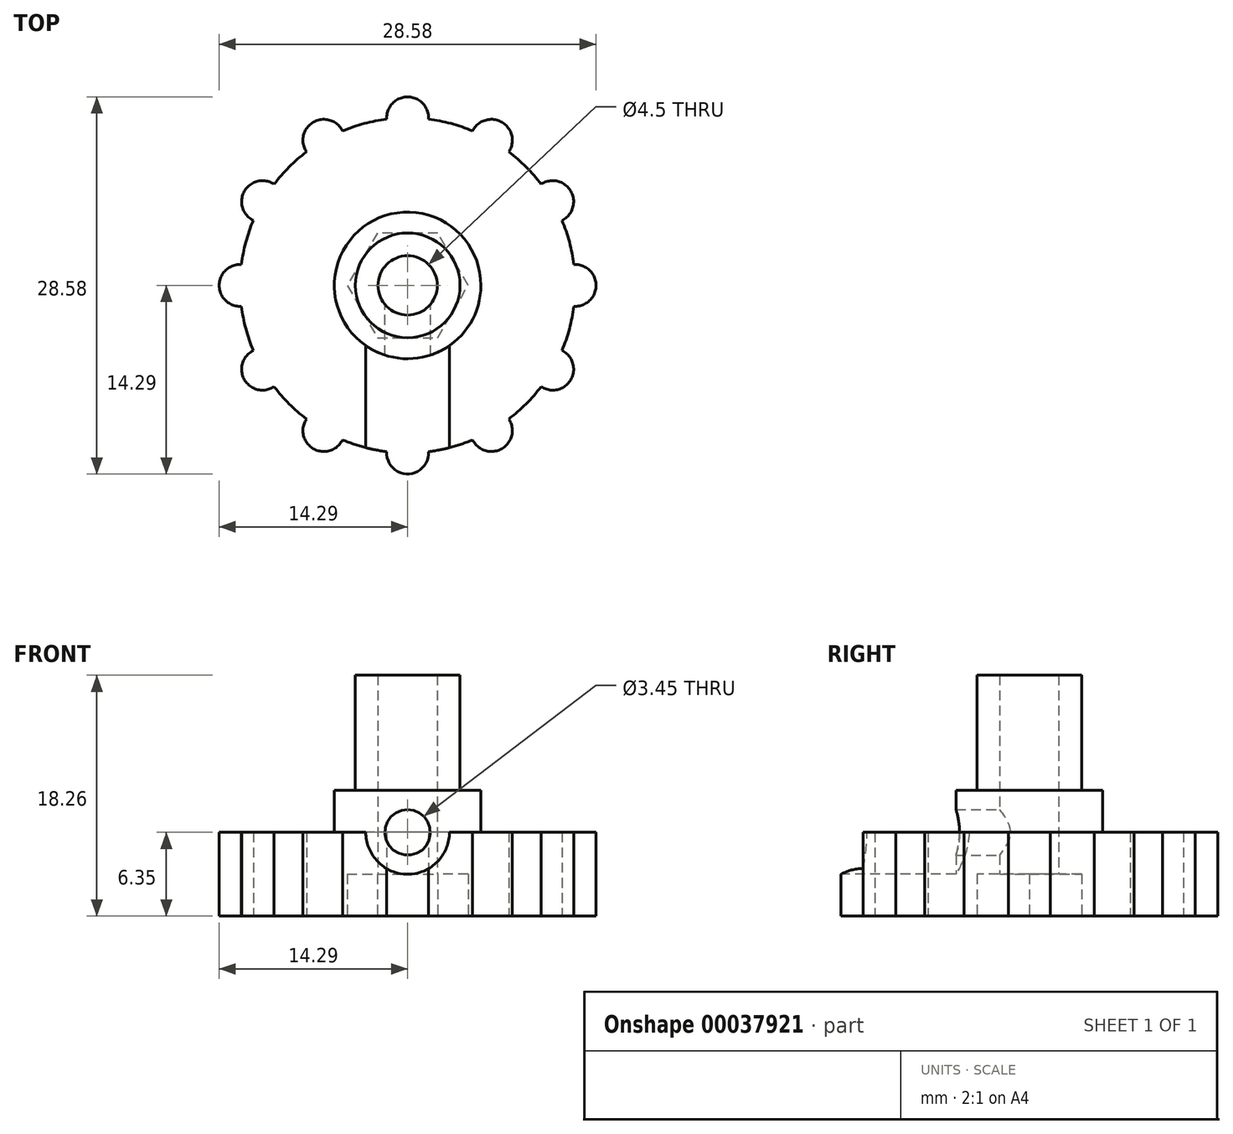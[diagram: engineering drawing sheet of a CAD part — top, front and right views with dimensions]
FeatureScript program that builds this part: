
annotation { "Feature Type Name" : "Feature", "Feature Type Description" : "" }
export const myFeature = defineFeature(function(context is Context, id is Id, definition is map)
    precondition{}
    {
        {
            var Q0;
            Q0=qCreatedBy(makeId("Top.planeOp"),FACE);
            var sketch = newSketch(context, id + "F0", { "sketchPlane" : qUnion([Q0])});
            skCircle(sketch, "E0", {"center": v(0, 0) * mm, "radius": 12.7 * mm});
            skSolve(sketch);
        }
        {
            var Q0;
            Q0=qSketchRegion(id+"F0",true);
            extrude(context, id + "F1", {"entities" : qUnion([Q0]), "depth" : 6.35 * mm});
        }
        {
            var Q0;
            Q0=makeQuery(id+"F1.opExtrude","CAP_FACE",FACE,{"disambiguationData":[OSD([sQuery(id+"F0.wireOp",EDGE,"E0")])],"isStart":true});
            var sketch = newSketch(context, id + "F2", { "sketchPlane" : qUnion([Q0])});
            skCircle(sketch, "E1.cCircle", {"center": v(0, 0) * mm, "radius": 3.97 * mm, "construction": true});
            skLineSegment(sketch, "E1.0", {"start": v(-2.3, 3.97) * mm, "end": v(2.3, 3.97) * mm});
            skLineSegment(sketch, "E1.1", {"start": v(2.3, 3.97) * mm, "end": v(4.58, 0) * mm});
            skLineSegment(sketch, "E1.2", {"start": v(4.58, 0) * mm, "end": v(2.3, -3.97) * mm});
            skLineSegment(sketch, "E1.3", {"start": v(2.3, -3.97) * mm, "end": v(-2.3, -3.97) * mm});
            skLineSegment(sketch, "E1.4", {"start": v(-2.3, -3.97) * mm, "end": v(-4.58, 0) * mm});
            skLineSegment(sketch, "E1.5", {"start": v(-4.58, 0) * mm, "end": v(-2.3, 3.97) * mm});
            skPoint(sketch, "E1.0.midPoint", {"position": v(0, 3.97) * mm});
            skSolve(sketch);
        }
        {
            var Q0;
            Q0=qSketchRegion(id+"F2",true);
            extrude(context, id + "F3", {"entities" : qUnion([Q0]), "operationType" : NewBodyOperationType.REMOVE, "oppositeDirection" : true, "depth" : 3.17 * mm});
        }
        {
            var Q0;
            Q0=makeQuery(id+"F1.opExtrude","CAP_FACE",FACE,{"disambiguationData":[OSD([sQuery(id+"F0.wireOp",EDGE,"E0")])],"isStart":false});
            var sketch = newSketch(context, id + "F4", { "sketchPlane" : qUnion([Q0])});
            skCircle(sketch, "E2", {"center": v(0, 0) * mm, "radius": 5.56 * mm});
            skSolve(sketch);
        }
        {
            var Q0;
            Q0=qSketchRegion(id+"F4",true);
            extrude(context, id + "F5", {"entities" : qUnion([Q0]), "operationType" : NewBodyOperationType.ADD, "depth" : 3.17 * mm});
        }
        {
            var Q0;
            Q0=makeQuery(id+"F5.opExtrude","CAP_FACE",FACE,{"disambiguationData":[OSD([sQuery(id+"F4.wireOp",EDGE,"E2")])],"isStart":false});
            var sketch = newSketch(context, id + "F6", { "sketchPlane" : qUnion([Q0])});
            skCircle(sketch, "E3", {"center": v(0, 0) * mm, "radius": 3.97 * mm});
            skSolve(sketch);
        }
        {
            var Q0;
            Q0=qSketchRegion(id+"F6",true);
            extrude(context, id + "F7", {"entities" : qUnion([Q0]), "operationType" : NewBodyOperationType.ADD, "depth" : 8.73 * mm});
        }
        {
            var Q0;
            Q0=makeQuery(id+"F3.boolean.opBoolean","COPY",FACE,{"derivedFrom":makeQuery(id+"F3.opExtrude","CAP_FACE",FACE,{"disambiguationData":[OSD([sQuery(id+"F2.wireOp",EDGE,"E1.0"),sQuery(id+"F2.wireOp",EDGE,"E1.1"),sQuery(id+"F2.wireOp",EDGE,"E1.2"),sQuery(id+"F2.wireOp",EDGE,"E1.3"),sQuery(id+"F2.wireOp",EDGE,"E1.4"),sQuery(id+"F2.wireOp",EDGE,"E1.5")])],"isStart":false})});
            var sketch = newSketch(context, id + "F8", { "sketchPlane" : qUnion([Q0])});
            skCircle(sketch, "E4", {"center": v(0, 0) * mm, "radius": 2.25 * mm});
            skSolve(sketch);
        }
        {
            var Q0;
            Q0=qSketchRegion(id+"F8",true);
            var Q1;
            Q1=makeQuery(id+"F7.opExtrude","CAP_FACE",FACE,{"disambiguationData":[OSD([sQuery(id+"F6.wireOp",EDGE,"E3")])],"isStart":false});
            extrude(context, id + "F9", {"entities" : qUnion([Q0]), "operationType" : NewBodyOperationType.REMOVE, "endBound" : BoundingType.UP_TO_SURFACE, "oppositeDirection" : true, "endBoundEntityFace" : qUnion([Q1]), "depth" : 25.4 * mm});
        }
        {
            var Q0;
            Q0=makeQuery(id+"F1.opExtrude","CAP_FACE",FACE,{"disambiguationData":[OSD([sQuery(id+"F0.wireOp",EDGE,"E0")])],"isStart":true});
            var sketch = newSketch(context, id + "F10", { "sketchPlane" : qUnion([Q0])});
            skArc(sketch, "E5", {"start": v(1.58, 12.6) * mm, "mid": v(0, 14.29) * mm, "end": v(-1.58, 12.6) * mm});
            skArc(sketch, "E6", {"start": v(1.58, 12.6) * mm, "mid": v(0, 12.7) * mm, "end": v(-1.58, 12.6) * mm});
            skSolve(sketch);
        }
        {
            var Q0;
            Q0=qSketchRegion(id+"F10",true);
            var Q1;
            Q1=makeQuery(id+"F1.opExtrude","CAP_FACE",FACE,{"disambiguationData":[OSD([sQuery(id+"F0.wireOp",EDGE,"E0")])],"isStart":false});
            extrude(context, id + "F11", {"entities" : qUnion([Q0]), "operationType" : NewBodyOperationType.ADD, "endBound" : BoundingType.UP_TO_SURFACE, "oppositeDirection" : true, "endBoundEntityFace" : qUnion([Q1]), "depth" : 25.4 * mm});
        }
        {
            var Q0;
            Q0=makeQuery(id+"F11.opExtrude","SWEPT_FACE",FACE,{"disambiguationData":[OSD([sQuery(id+"F10.wireOp",EDGE,"E5")])]});
            var Q1;
            Q1=makeQuery(id+"F1.opExtrude","SWEPT_FACE",FACE,{"disambiguationData":[OSD([sQuery(id+"F0.wireOp",EDGE,"E0")])]});
            circularPattern(context, id + "F12", {"operationType" : NewBodyOperationType.ADD, "faces" : qUnion([Q0]), "axis" : qUnion([Q1]), "angle" : 30 * degree, "instanceCount" : round(12), "patternType" : PatternType.FACE});
        }
        {
            var Q0;
            Q0=qCreatedBy(makeId("Front.planeOp"),FACE);
            var sketch = newSketch(context, id + "F13", { "sketchPlane" : qUnion([Q0])});
            skLineSegment(sketch, "E7", {"start": v(0, 3.18) * mm, "end": v(0, 9.53) * mm});
            skCircle(sketch, "E8", {"center": v(0, 6.35) * mm, "radius": 1.73 * mm});
            skSolve(sketch);
        }
        {
            var Q0;
            Q0=qSketchRegion(id+"F13",true);
            var Q1;
            Q1=makeQuery(id+"F5.opExtrude","SWEPT_FACE",FACE,{"disambiguationData":[OSD([sQuery(id+"F4.wireOp",EDGE,"E2")])]});
            extrude(context, id + "F14", {"entities" : qUnion([Q0]), "operationType" : NewBodyOperationType.REMOVE, "endBound" : BoundingType.UP_TO_SURFACE, "endBoundEntityFace" : qUnion([Q1]), "depth" : 25.4 * mm});
        }
        {
            var Q0;
            Q0=qCreatedBy(makeId("Front.planeOp"),FACE);
            cPlane(context, id + "F15", {"entities" : qUnion([Q0]), "cplaneType" : CPlaneType.OFFSET, "offset" : 14.29 * mm, "width" : 152.4 * mm, "height" : 152.4 * mm});
        }
        {
            var Q0;
            Q0=qCreatedBy(id+"F15.planeOp",FACE);
            var sketch = newSketch(context, id + "F16", { "sketchPlane" : qUnion([Q0])});
            skArc(sketch, "E9", {"start": v(3.17, 6.35) * mm, "mid": v(0, 9.53) * mm, "end": v(-3.18, 6.35) * mm, "construction": true});
            skArc(sketch, "E10", {"start": v(-3.18, 6.35) * mm, "mid": v(0, 3.17) * mm, "end": v(3.17, 6.35) * mm});
            skLineSegment(sketch, "E11", {"start": v(-3.18, 6.35) * mm, "end": v(3.17, 6.35) * mm});
            skSolve(sketch);
        }
        {
            var Q0;
            Q0=qSketchRegion(id+"F16",true);
            var Q1;
            Q1=makeQuery(id+"F5.opExtrude","SWEPT_FACE",FACE,{"disambiguationData":[OSD([sQuery(id+"F4.wireOp",EDGE,"E2")])]});
            extrude(context, id + "F17", {"entities" : qUnion([Q0]), "operationType" : NewBodyOperationType.REMOVE, "endBound" : BoundingType.UP_TO_SURFACE, "oppositeDirection" : true, "endBoundEntityFace" : qUnion([Q1]), "depth" : 25.4 * mm});
        }
    });
